# Revit family: 317_796e458a62c146dca4ce5ce7824272
name_source: partatom
category: Mechanical Equipment
units: mm (PartAtom-declared; Revit-internal decimal feet)

## family parameters
Always vertical = Yes
Cut with Voids When Loaded = No
Part Type = Normal
Room Calculation Point = No
Round Connector Dimension = Use Diameter
Shared = No
Work Plane-Based = No

## types (1)
- VMC322 G1 45-50-60°C
    A = 32 mm  [stored 0.104987 ft]
    A1 = 2 mm  [stored 0.00656168 ft]
    A2 = 19 mm  [stored 0.062336 ft]
    A3 = 18 mm
    A4 = 14 mm  [stored 0.0459318 ft]
    A5 = 13 mm  [stored 0.0426509 ft]
    A__ve = -32 mm  [stored -0.104987 ft]
    B = 42 mm  [stored 0.137795 ft]
    B1 = 28 mm
    C = 52 mm  [stored 0.170604 ft]
    CAT0 = Yes
    CenSd_DN1_6 = 16 mm  [stored 0.0524934 ft]
    D = 25 mm
    DN1 = 19 mm  [stored 0.062336 ft]
    DT2 = 13 mm  [stored 0.0426509 ft]
    Description = Solar kit VMC322, PN10 external thread
    E = 42 mm  [stored 0.137795 ft]
    ET2 = 17 mm
    F = 42 mm  [stored 0.137795 ft]
    G = 35 mm
    H = 68 mm  [stored 0.223097 ft]
    H3 = 94 mm  [stored 0.308399 ft]
    H3__ve = -94 mm  [stored -0.308399 ft]
    J = 136 mm  [stored 0.446194 ft]
    LT2 = 95 mm  [stored 0.31168 ft]
    MC Product Code = VMC322 G1 45-50-60°C
    Manufacturer = ESBE
    QmdConnectorList = 321;D;322;D;351;D;352;D
    R1 = 11 mm
    R11 = 11 mm
    URL = http://www.esbe.eu
    WT2 = 23 mm  [stored 0.0754593 ft]
    X1 = 8 mm  [stored 0.0262467 ft]
    X1__ve = -8 mm  [stored -0.0262467 ft]
    X2 = 50 mm  [stored 0.164042 ft]
    X3 = 15 mm  [stored 0.0492126 ft]
    X4 = 49 mm  [stored 0.160761 ft]
    X5 = 50 mm  [stored 0.164042 ft]
    X6 = 46 mm  [stored 0.150919 ft]
    X7 = 42 mm  [stored 0.137795 ft]
    Z1 = 32 mm  [stored 0.104987 ft]
    Z3 = 4 mm  [stored 0.0131234 ft]
    Z4 = 11 mm
    Z5 = 32 mm  [stored 0.104987 ft]
    Z5__ve = -32 mm  [stored -0.104987 ft]
    magiPartTypeId = 317
    magiProductFamilyId = 796e458a62c146dca4ce5ce7824272
    magiProductId = 796e458a62c146dca4ce5ce7824272

note: [stored X ft] marks values corroborated as IEEE doubles in the binary element streams (Revit-internal decimal feet)

## geometry (parser evidence)
native form markers: Sweep x2
no freeform markers — native parametric forms only
